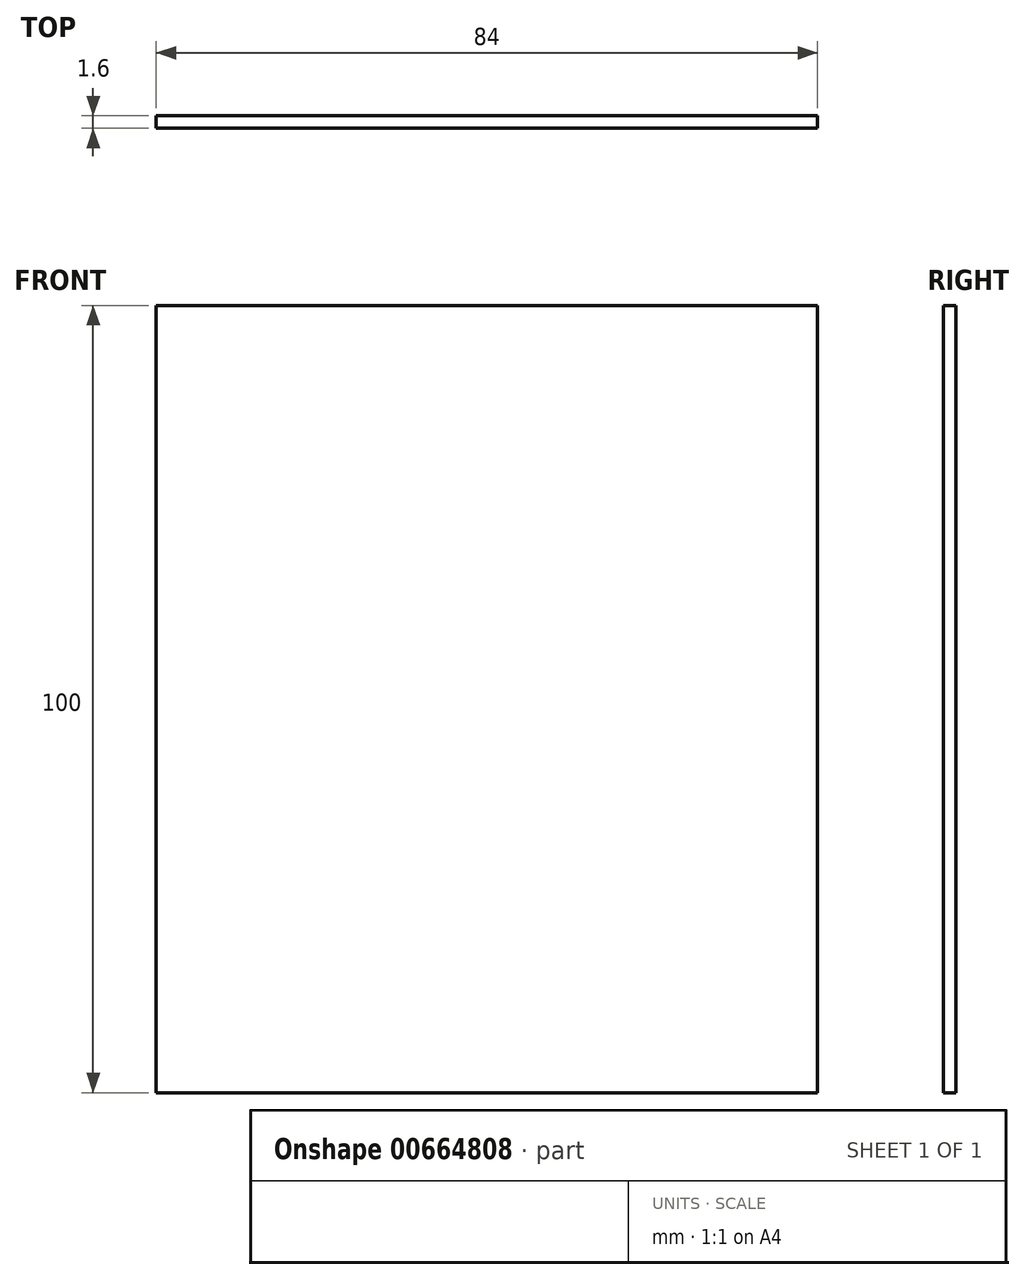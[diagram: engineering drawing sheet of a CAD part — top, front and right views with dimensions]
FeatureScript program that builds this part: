
annotation { "Feature Type Name" : "Feature", "Feature Type Description" : "" }
export const myFeature = defineFeature(function(context is Context, id is Id, definition is map)
    precondition{}
    {
        {
            var Q0;
            Q0=qCreatedBy(makeId("Front.planeOp"),FACE);
            var sketch = newSketch(context, id + "F0", { "sketchPlane" : qUnion([Q0])});
            skLineSegment(sketch, "E0.bottom", {"start": v(42, 50) * mm, "end": v(-42, 50) * mm});
            skLineSegment(sketch, "E0.top", {"start": v(42, -50) * mm, "end": v(-42, -50) * mm});
            skLineSegment(sketch, "E0.left", {"start": v(42, 50) * mm, "end": v(42, -50) * mm});
            skLineSegment(sketch, "E0.right", {"start": v(-42, 50) * mm, "end": v(-42, -50) * mm});
            skPoint(sketch, "E0.middle", {"position": v(0, 0) * mm});
            skSolve(sketch);
        }
        {
            var Q0;
            Q0=makeQuery(id+"F0.imprint","IMPRINT",FACE,{"disambiguationData":[TD([[makeQuery(id+"F0.imprint","IMPRINT",EDGE,{"derivedFrom":sQuery(id+"F0.wireOp",EDGE,"E0.bottom")}),1.0]])]});
            extrude(context, id + "F1", {"entities" : qUnion([Q0]), "depth" : .8 * mm, "offsetDistance" : 25 * mm, "hasSecondDirection" : true, "secondDirectionOppositeDirection" : true, "secondDirectionDepth" : .8 * mm});
        }
    });
